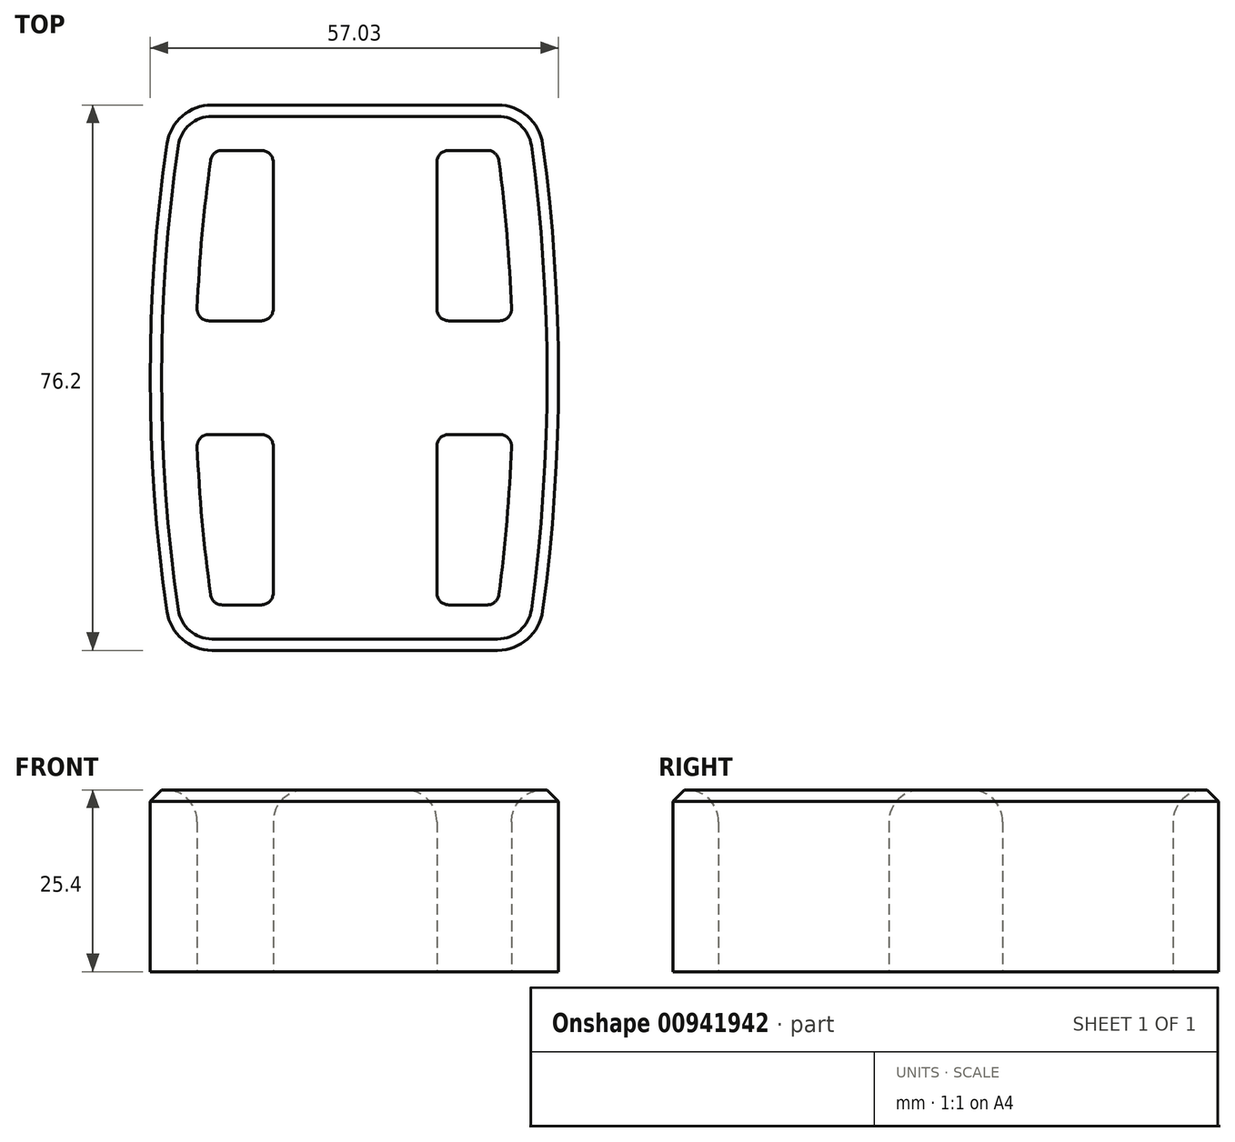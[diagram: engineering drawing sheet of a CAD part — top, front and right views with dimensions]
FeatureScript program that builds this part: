
annotation { "Feature Type Name" : "Feature", "Feature Type Description" : "" }
export const myFeature = defineFeature(function(context is Context, id is Id, definition is map)
    precondition{}
    {
        {
            var Q0;
            Q0=qCreatedBy(makeId("Top.planeOp"),FACE);
            var sketch = newSketch(context, id + "F0", { "sketchPlane" : qUnion([Q0])});
            skLineSegment(sketch, "E0.bottom", {"start": v(19.92, 38.1) * mm, "end": v(-19.97, 38.1) * mm});
            skLineSegment(sketch, "E0.top", {"start": v(19.92, -38.1) * mm, "end": v(-19.97, -38.1) * mm});
            skPoint(sketch, "E0.middle", {"position": v(0, 0) * mm});
            skArc(sketch, "E1", {"start": v(-26.26, 32.66) * mm, "mid": v(-28.62, 0) * mm, "end": v(-26.26, -32.66) * mm});
            skArc(sketch, "E2", {"start": v(26.2, -32.6) * mm, "mid": v(28.4, 0) * mm, "end": v(26.2, 32.6) * mm});
            skLineSegment(sketch, "E3.0", {"start": v(18.47, -31.75) * mm, "end": v(13.08, -31.75) * mm});
            skArc(sketch, "E3.1", {"start": v(20.1, -30.31) * mm, "mid": v(21.21, -20) * mm, "end": v(21.86, -9.66) * mm});
            skLineSegment(sketch, "E4.0", {"start": v(18.47, 31.75) * mm, "end": v(13.08, 31.75) * mm});
            skArc(sketch, "E5.0", {"start": v(-20.18, 30.33) * mm, "mid": v(-21.36, 20.02) * mm, "end": v(-22.06, 9.66) * mm});
            skLineSegment(sketch, "E6.left", {"start": v(11.43, 30.1) * mm, "end": v(11.43, 9.59) * mm});
            skLineSegment(sketch, "E6.right", {"start": v(-11.43, 30.1) * mm, "end": v(-11.43, 9.59) * mm});
            skLineSegment(sketch, "E7.bottom", {"start": v(20.21, 7.94) * mm, "end": v(13.08, 7.94) * mm});
            skLineSegment(sketch, "E7.top", {"start": v(20.21, -7.94) * mm, "end": v(13.08, -7.94) * mm});
            skArc(sketch, "E8.trimOffspring", {"start": v(-22.06, -9.66) * mm, "mid": v(-21.36, -20.02) * mm, "end": v(-20.18, -30.33) * mm});
            skLineSegment(sketch, "E9.trimOffspring", {"start": v(-11.43, -9.59) * mm, "end": v(-11.43, -30.1) * mm});
            skLineSegment(sketch, "E10.trimOffspring", {"start": v(11.43, -9.59) * mm, "end": v(11.43, -30.1) * mm});
            skArc(sketch, "E11.trimOffspring", {"start": v(21.86, 9.66) * mm, "mid": v(21.21, 20) * mm, "end": v(20.1, 30.31) * mm});
            skLineSegment(sketch, "E12.trimOffspring", {"start": v(-13.08, 7.94) * mm, "end": v(-20.4, 7.94) * mm});
            skLineSegment(sketch, "E13.trimOffspring", {"start": v(-13.08, 31.75) * mm, "end": v(-18.54, 31.75) * mm});
            skLineSegment(sketch, "E14.trimOffspring", {"start": v(-13.08, -7.94) * mm, "end": v(-20.4, -7.94) * mm});
            skLineSegment(sketch, "E15.trimOffspring", {"start": v(-13.08, -31.75) * mm, "end": v(-18.54, -31.75) * mm});
            skPoint(sketch, "E7.right.end.orphan", {"position": v(-28.28, -7.94) * mm});
            skPoint(sketch, "E7.right.start.orphan", {"position": v(-28.28, 7.94) * mm});
            skPoint(sketch, "E7.left.end.orphan", {"position": v(28.28, -7.94) * mm});
            skPoint(sketch, "E7.left.start.orphan", {"position": v(28.28, 7.94) * mm});
            skPoint(sketch, "E16.visualSharp", {"position": v(-11.43, 7.94) * mm});
            skArc(sketch, "E16.filletArc", {"start": v(-13.08, 7.94) * mm, "mid": v(-11.91, 8.42) * mm, "end": v(-11.43, 9.59) * mm});
            skPoint(sketch, "E17.visualSharp", {"position": v(-11.43, 31.75) * mm});
            skArc(sketch, "E17.filletArc", {"start": v(-11.43, 30.1) * mm, "mid": v(-11.91, 31.27) * mm, "end": v(-13.08, 31.75) * mm});
            skPoint(sketch, "E18.visualSharp", {"position": v(-19.97, 31.75) * mm});
            skArc(sketch, "E18.filletArc", {"start": v(-18.54, 31.75) * mm, "mid": v(-19.63, 31.34) * mm, "end": v(-20.18, 30.33) * mm});
            skPoint(sketch, "E19.visualSharp", {"position": v(-22.13, 7.94) * mm});
            skArc(sketch, "E19.filletArc", {"start": v(-22.06, 9.66) * mm, "mid": v(-21.6, 8.45) * mm, "end": v(-20.4, 7.94) * mm});
            skPoint(sketch, "E20.visualSharp", {"position": v(11.43, 7.94) * mm});
            skArc(sketch, "E20.filletArc", {"start": v(11.43, 9.59) * mm, "mid": v(11.91, 8.42) * mm, "end": v(13.08, 7.94) * mm});
            skPoint(sketch, "E21.visualSharp", {"position": v(11.43, 31.75) * mm});
            skArc(sketch, "E21.filletArc", {"start": v(13.08, 31.75) * mm, "mid": v(11.91, 31.27) * mm, "end": v(11.43, 30.1) * mm});
            skPoint(sketch, "E22.visualSharp", {"position": v(19.92, 31.75) * mm});
            skArc(sketch, "E22.filletArc", {"start": v(20.1, 30.31) * mm, "mid": v(19.56, 31.34) * mm, "end": v(18.47, 31.75) * mm});
            skPoint(sketch, "E23.visualSharp", {"position": v(21.93, 7.94) * mm});
            skArc(sketch, "E23.filletArc", {"start": v(20.21, 7.94) * mm, "mid": v(21.4, 8.45) * mm, "end": v(21.86, 9.66) * mm});
            skPoint(sketch, "E24.visualSharp", {"position": v(-11.43, -7.94) * mm});
            skArc(sketch, "E24.filletArc", {"start": v(-11.43, -9.59) * mm, "mid": v(-11.91, -8.42) * mm, "end": v(-13.08, -7.94) * mm});
            skPoint(sketch, "E25.visualSharp", {"position": v(-22.13, -7.94) * mm});
            skArc(sketch, "E25.filletArc", {"start": v(-20.4, -7.94) * mm, "mid": v(-21.6, -8.45) * mm, "end": v(-22.06, -9.66) * mm});
            skPoint(sketch, "E26.visualSharp", {"position": v(-11.43, -31.75) * mm});
            skArc(sketch, "E26.filletArc", {"start": v(-13.08, -31.75) * mm, "mid": v(-11.91, -31.27) * mm, "end": v(-11.43, -30.1) * mm});
            skPoint(sketch, "E27.visualSharp", {"position": v(-19.97, -31.75) * mm});
            skArc(sketch, "E27.filletArc", {"start": v(-20.18, -30.33) * mm, "mid": v(-19.63, -31.34) * mm, "end": v(-18.54, -31.75) * mm});
            skPoint(sketch, "E28.visualSharp", {"position": v(11.43, -31.75) * mm});
            skArc(sketch, "E28.filletArc", {"start": v(11.43, -30.1) * mm, "mid": v(11.91, -31.27) * mm, "end": v(13.08, -31.75) * mm});
            skPoint(sketch, "E29.visualSharp", {"position": v(19.92, -31.75) * mm});
            skArc(sketch, "E29.filletArc", {"start": v(18.47, -31.75) * mm, "mid": v(19.56, -31.34) * mm, "end": v(20.1, -30.31) * mm});
            skPoint(sketch, "E30.visualSharp", {"position": v(21.93, -7.94) * mm});
            skArc(sketch, "E30.filletArc", {"start": v(21.86, -9.66) * mm, "mid": v(21.4, -8.45) * mm, "end": v(20.21, -7.94) * mm});
            skPoint(sketch, "E31.visualSharp", {"position": v(11.43, -7.94) * mm});
            skArc(sketch, "E31.filletArc", {"start": v(13.08, -7.94) * mm, "mid": v(11.91, -8.42) * mm, "end": v(11.43, -9.59) * mm});
            skPoint(sketch, "E32.visualSharp", {"position": v(25.4, -38.1) * mm});
            skArc(sketch, "E32.filletArc", {"start": v(19.92, -38.1) * mm, "mid": v(24.1, -36.53) * mm, "end": v(26.2, -32.6) * mm});
            skPoint(sketch, "E33.visualSharp", {"position": v(-25.4, -38.1) * mm});
            skArc(sketch, "E33.filletArc", {"start": v(-26.26, -32.66) * mm, "mid": v(-24.13, -36.55) * mm, "end": v(-19.97, -38.1) * mm});
            skPoint(sketch, "E34.visualSharp", {"position": v(-25.4, 38.1) * mm});
            skArc(sketch, "E34.filletArc", {"start": v(-19.97, 38.1) * mm, "mid": v(-24.13, 36.55) * mm, "end": v(-26.26, 32.66) * mm});
            skPoint(sketch, "E35.visualSharp", {"position": v(25.4, 38.1) * mm});
            skArc(sketch, "E35.filletArc", {"start": v(26.2, 32.6) * mm, "mid": v(24.1, 36.53) * mm, "end": v(19.92, 38.1) * mm});
            skSolve(sketch);
        }
        {
            var Q0;
            Q0=makeQuery(id+"F0.imprint","IMPRINT",FACE,{"disambiguationData":[TD([[makeQuery(id+"F0.imprint","IMPRINT",EDGE,{"derivedFrom":sQuery(id+"F0.wireOp",EDGE,"E0.bottom")}),1.0]])]});
            extrude(context, id + "F1", {"entities" : qUnion([Q0]), "endBound" : BoundingType.SYMMETRIC, "depth" : 25.4 * mm, "offsetDistance" : 25.4 * mm});
        }
        {
            var Q0;
            Q0=makeQuery(id+"F1.opExtrude","CAP_EDGE",EDGE,{"disambiguationData":[OSD([sQuery(id+"F0.wireOp",EDGE,"E10.trimOffspring")])],"isStart":false});
            var Q1;
            Q1=makeQuery(id+"F1.opExtrude","CAP_EDGE",EDGE,{"disambiguationData":[OSD([sQuery(id+"F0.wireOp",EDGE,"E9.trimOffspring")])],"isStart":false});
            var Q2;
            Q2=makeQuery(id+"F1.opExtrude","CAP_EDGE",EDGE,{"disambiguationData":[OSD([sQuery(id+"F0.wireOp",EDGE,"E6.left")])],"isStart":false});
            var Q3;
            Q3=makeQuery(id+"F1.opExtrude","CAP_EDGE",EDGE,{"disambiguationData":[OSD([sQuery(id+"F0.wireOp",EDGE,"E6.right")])],"isStart":false});
            fillet(context, id + "F2", {"entities" : qUnion([Q0, Q1, Q2, Q3]), "radius" : 4.44 * mm, "tangentPropagation" : true, "allowEdgeOverflow" : false});
        }
        {
            var Q0;
            Q0=makeQuery(id+"F1.opExtrude","CAP_EDGE",EDGE,{"disambiguationData":[OSD([sQuery(id+"F0.wireOp",EDGE,"E0.top")])],"isStart":false});
            chamfer(context, id + "F3", {"entities" : qUnion([Q0]), "width" : 1.59 * mm, "tangentPropagation" : true});
        }
    });
